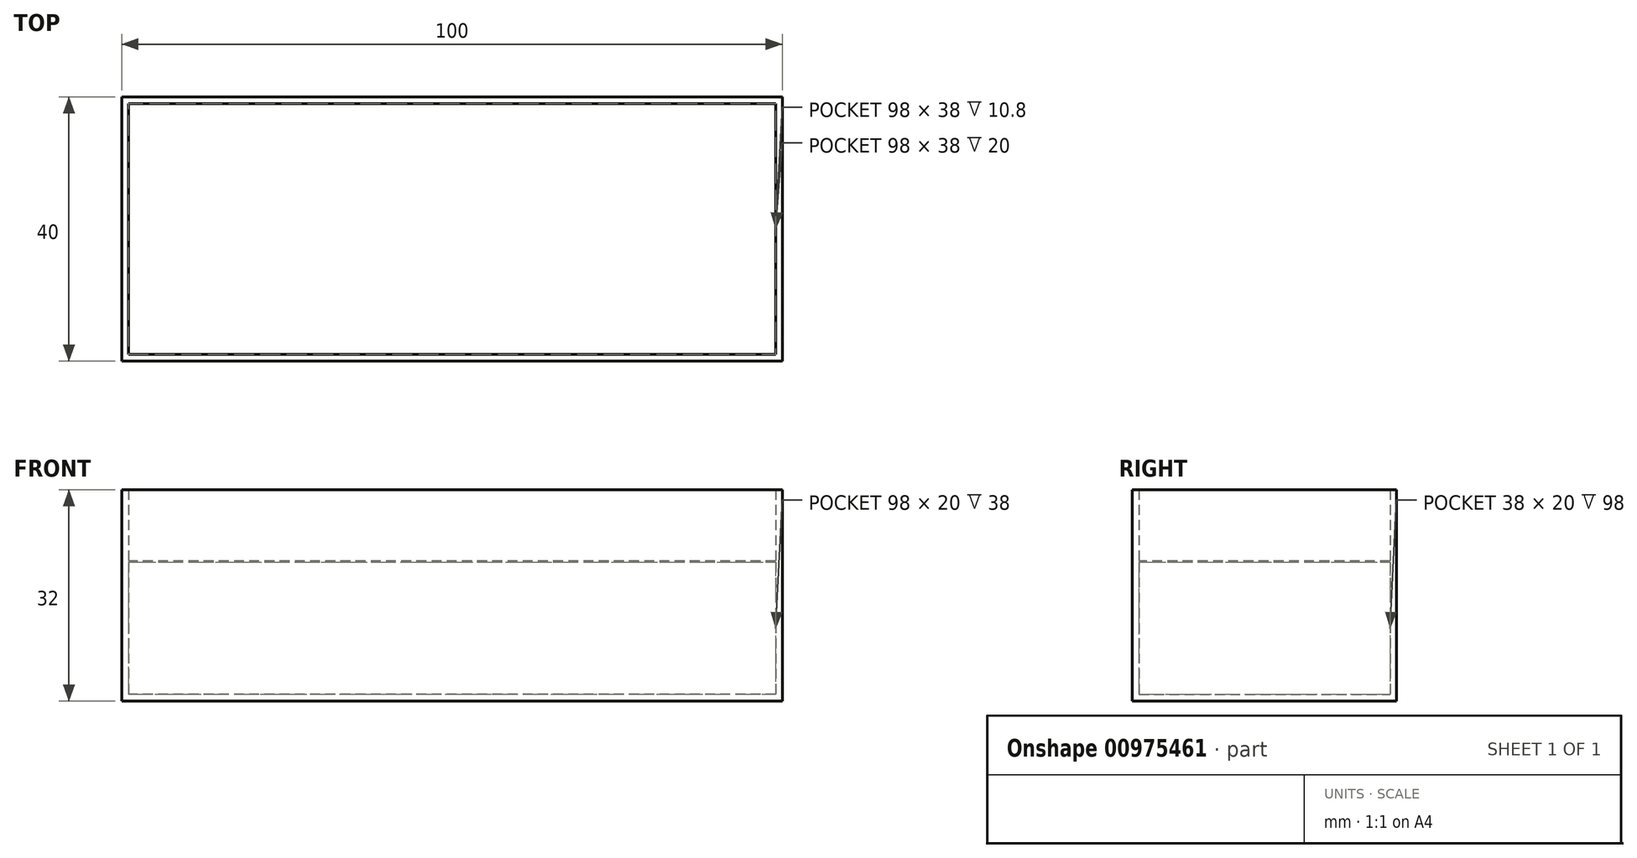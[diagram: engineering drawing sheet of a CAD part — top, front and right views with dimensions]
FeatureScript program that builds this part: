
annotation { "Feature Type Name" : "Feature", "Feature Type Description" : "" }
export const myFeature = defineFeature(function(context is Context, id is Id, definition is map)
    precondition{}
    {
        {
            var Q0;
            Q0=qCreatedBy(makeId("Top.planeOp"),FACE);
            var sketch = newSketch(context, id + "F0", { "sketchPlane" : qUnion([Q0])});
            skLineSegment(sketch, "E0.bottom", {"start": v(50, -20) * mm, "end": v(-50, -20) * mm});
            skLineSegment(sketch, "E0.top", {"start": v(50, 20) * mm, "end": v(-50, 20) * mm});
            skLineSegment(sketch, "E0.left", {"start": v(50, -20) * mm, "end": v(50, 20) * mm});
            skLineSegment(sketch, "E0.right", {"start": v(-50, -20) * mm, "end": v(-50, 20) * mm});
            skPoint(sketch, "E0.middle", {"position": v(0, 0) * mm});
            skSolve(sketch);
        }
        {
            var Q0;
            Q0=makeQuery(id+"F0.imprint","IMPRINT",FACE,{"disambiguationData":[TD([[makeQuery(id+"F0.imprint","IMPRINT",EDGE,{"derivedFrom":sQuery(id+"F0.wireOp",EDGE,"E0.bottom")}),-1.0]])]});
            extrude(context, id + "F1", {"entities" : qUnion([Q0]), "depth" : 32 * mm, "offsetDistance" : 25 * mm});
        }
        {
            var Q0;
            Q0=makeQuery(id+"F1.opExtrude","CAP_FACE",FACE,{"disambiguationData":[OSD([sQuery(id+"F0.wireOp",EDGE,"E0.bottom"),sQuery(id+"F0.wireOp",EDGE,"E0.top"),sQuery(id+"F0.wireOp",EDGE,"E0.left"),sQuery(id+"F0.wireOp",EDGE,"E0.right")])],"isStart":false});
            shell(context, id + "F2", {"entities" : qUnion([Q0]), "thickness" : 1 * mm});
        }
        {
            var Q0;
            Q0=makeQuery(id+"F2.opShell","OFFSET_FACE",FACE,{"disambiguationData":[OSD([sQuery(id+"F0.wireOp",EDGE,"E0.right")])]});
            var sketch = newSketch(context, id + "F3", { "sketchPlane" : qUnion([Q0])});
            skLineSegment(sketch, "E1.bottom", {"start": v(-19, 21.2) * mm, "end": v(19, 21.2) * mm});
            skLineSegment(sketch, "E1.top", {"start": v(-19, 21) * mm, "end": v(19, 21) * mm});
            skLineSegment(sketch, "E1.left", {"start": v(-19, 21.2) * mm, "end": v(-19, 21) * mm});
            skLineSegment(sketch, "E1.right", {"start": v(19, 21.2) * mm, "end": v(19, 21) * mm});
            skSolve(sketch);
        }
        {
            var Q0;
            Q0 = qSketchRegion(id + "F3", true);
            extrude(context, id + "F4", {"entities" : qUnion([Q0]), "operationType" : NewBodyOperationType.ADD, "endBound" : BoundingType.UP_TO_NEXT, "depth" : 25 * mm, "offsetDistance" : 25 * mm});
        }
    });
